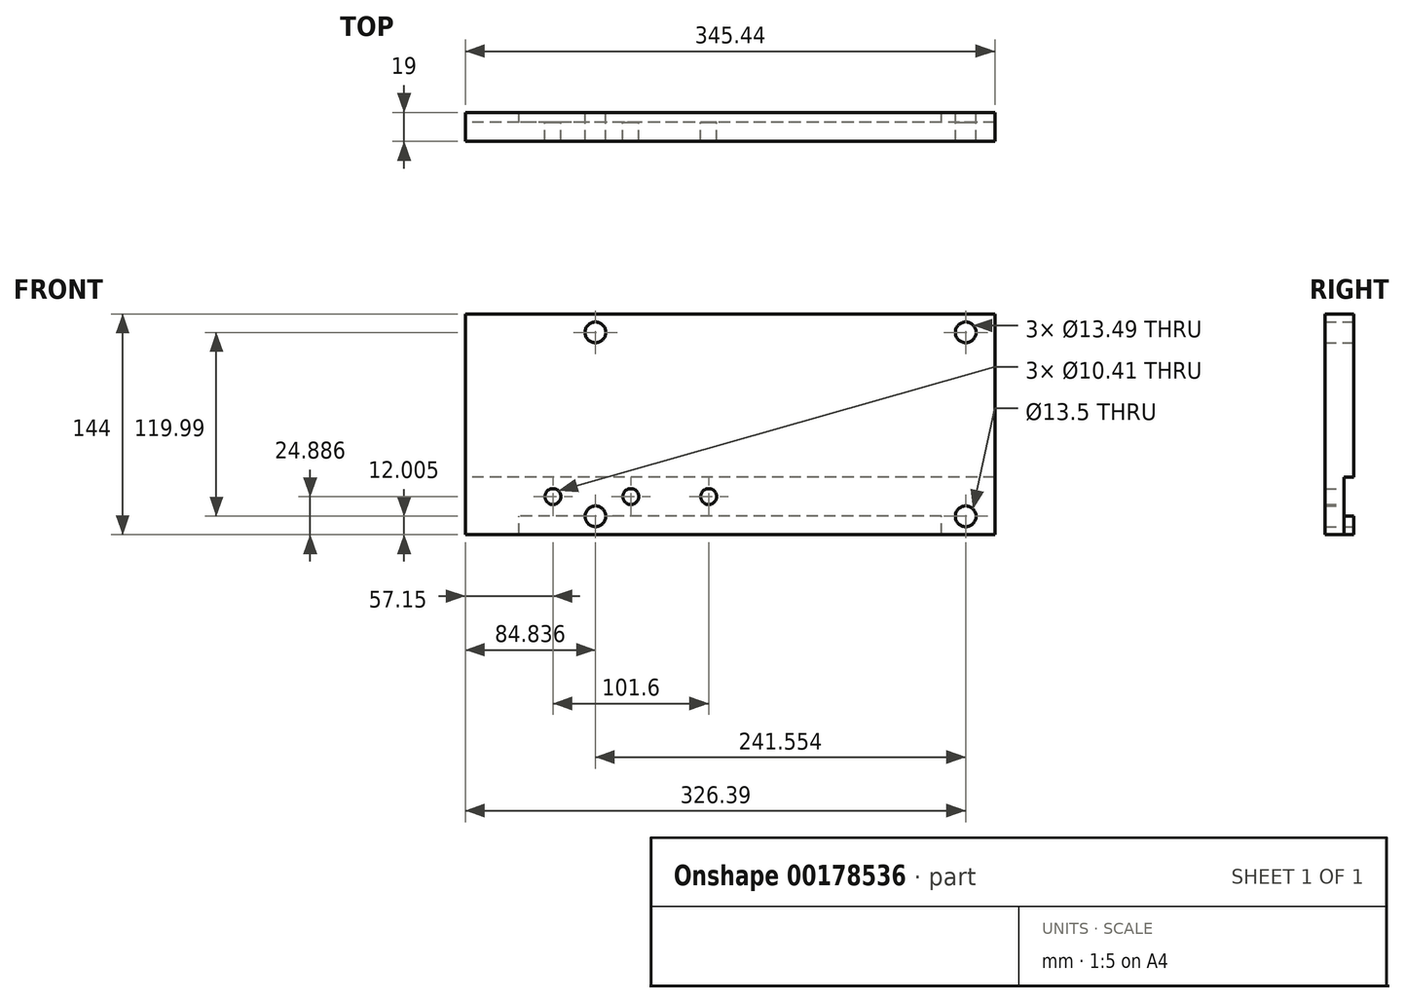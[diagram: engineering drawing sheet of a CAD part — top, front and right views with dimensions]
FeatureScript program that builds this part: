
annotation { "Feature Type Name" : "Feature", "Feature Type Description" : "" }
export const myFeature = defineFeature(function(context is Context, id is Id, definition is map)
    precondition{}
    {
        {
            var Q0;
            Q0=qCreatedBy(makeId("Front.planeOp"),FACE);
            var sketch = newSketch(context, id + "F0", { "sketchPlane" : qUnion([Q0])});
            skLineSegment(sketch, "E0.bottom", {"start": v(172.72, 72) * mm, "end": v(-172.72, 72) * mm});
            skLineSegment(sketch, "E0.top", {"start": v(172.72, -72) * mm, "end": v(-172.72, -72) * mm});
            skLineSegment(sketch, "E0.left", {"start": v(172.72, 72) * mm, "end": v(172.72, -72) * mm});
            skLineSegment(sketch, "E0.right", {"start": v(-172.72, 72) * mm, "end": v(-172.72, -72) * mm});
            skPoint(sketch, "E0.middle", {"position": v(0, 0) * mm});
            skCircle(sketch, "E1", {"center": v(-115.57, -47.11) * mm, "radius": 5.2 * mm});
            skCircle(sketch, "E2.1.0.0", {"center": v(-64.77, -47.11) * mm, "radius": 5.2 * mm});
            skCircle(sketch, "E2.2.0.0", {"center": v(-13.97, -47.11) * mm, "radius": 5.2 * mm});
            skLineSegment(sketch, "E2.direction1", {"start": v(-115.57, -47.11) * mm, "end": v(-64.77, -47.11) * mm, "construction": true});
            skCircle(sketch, "E3", {"center": v(153.67, -60) * mm, "radius": 6.75 * mm});
            skCircle(sketch, "E4", {"center": v(153.67, 60) * mm, "radius": 6.74 * mm});
            skCircle(sketch, "E5", {"center": v(-87.88, -60) * mm, "radius": 6.74 * mm});
            skCircle(sketch, "E6", {"center": v(-87.88, 60) * mm, "radius": 6.74 * mm});
            skSolve(sketch);
        }
        {
            var Q0;
            Q0 = qSketchRegion(id + "F0", true);
            extrude(context, id + "F1", {"entities" : qUnion([Q0]), "depth" : 19 * mm});
        }
        {
            var Q0;
            Q0=makeQuery(id+"F1.opExtrude","SWEPT_FACE",FACE,{"disambiguationData":[OSD([sQuery(id+"F0.wireOp",EDGE,"E0.right")])]});
            var sketch = newSketch(context, id + "F2", { "sketchPlane" : qUnion([Q0])});
            skLineSegment(sketch, "E7.right", {"start": v(6.35, -59.81) * mm, "end": v(6.35, -34.41) * mm});
            skLineSegment(sketch, "E8", {"start": v(6.35, -59.81) * mm, "end": v(0, -59.81) * mm});
            skLineSegment(sketch, "E9", {"start": v(0, -59.81) * mm, "end": v(0, -34.41) * mm});
            skLineSegment(sketch, "E10", {"start": v(0, -34.41) * mm, "end": v(6.35, -34.41) * mm});
            skSolve(sketch);
        }
        {
            var Q0;
            Q0 = qSketchRegion(id + "F2", true);
            extrude(context, id + "F3", {"entities" : qUnion([Q0]), "operationType" : NewBodyOperationType.REMOVE, "endBound" : BoundingType.THROUGH_ALL, "oppositeDirection" : true, "depth" : 25.4 * mm});
        }
        {
            var Q0;
            {var subQ0=sQuery(id+"F0.wireOp",EDGE,"E0.right");var subQ1=sQuery(id+"F0.wireOp",EDGE,"E0.left");var subQ2=sQuery(id+"F0.wireOp",EDGE,"E3");var subQ3=sQuery(id+"F0.wireOp",EDGE,"E0.top");var subQ4=sQuery(id+"F0.wireOp",EDGE,"E5");Q0=makeQuery(id+"F3.boolean.opBoolean","SPLIT",FACE,{"disambiguationData":[TD([makeQuery(id+"F1.opExtrude","SWEPT_FACE",FACE,{"disambiguationData":[OSD([subQ3])]})])],"derivedFrom":makeQuery(id+"F1.opExtrude","CAP_FACE",FACE,{"disambiguationData":[OSD([sQuery(id+"F0.wireOp",EDGE,"E0.bottom"),subQ3,subQ1,subQ0,sQuery(id+"F0.wireOp",EDGE,"E1"),sQuery(id+"F0.wireOp",EDGE,"E2.1.0.0"),sQuery(id+"F0.wireOp",EDGE,"E2.2.0.0"),subQ2,sQuery(id+"F0.wireOp",EDGE,"E4"),subQ4,sQuery(id+"F0.wireOp",EDGE,"E6")])],"isStart":true})});}
            var sketch = newSketch(context, id + "F4", { "sketchPlane" : qUnion([Q0])});
            skLineSegment(sketch, "E11.bottom", {"start": v(-172.72, -72) * mm, "end": v(-137.8, -72) * mm});
            skLineSegment(sketch, "E11.top", {"start": v(-172.72, -34.41) * mm, "end": v(-137.8, -34.41) * mm});
            skLineSegment(sketch, "E11.left", {"start": v(-172.72, -72) * mm, "end": v(-172.72, -34.41) * mm});
            skLineSegment(sketch, "E11.right", {"start": v(-137.8, -72) * mm, "end": v(-137.8, -34.41) * mm});
            skLineSegment(sketch, "E12.bottom", {"start": v(172.72, -72) * mm, "end": v(137.8, -72) * mm});
            skLineSegment(sketch, "E12.top", {"start": v(172.72, -34.41) * mm, "end": v(137.8, -34.41) * mm});
            skLineSegment(sketch, "E12.left", {"start": v(172.72, -72) * mm, "end": v(172.72, -34.41) * mm});
            skLineSegment(sketch, "E12.right", {"start": v(137.8, -72) * mm, "end": v(137.8, -34.41) * mm});
            skSolve(sketch);
        }
        {
            var Q0;
            Q0 = qSketchRegion(id + "F4", true);
            var Q1;
            Q1=makeQuery(id+"F3.boolean.opBoolean","COPY",FACE,{"derivedFrom":makeQuery(id+"F3.opExtrude","SWEPT_FACE",FACE,{"disambiguationData":[OSD([sQuery(id+"F2.wireOp",EDGE,"E7.right")])]})});
            extrude(context, id + "F5", {"entities" : qUnion([Q0]), "operationType" : NewBodyOperationType.REMOVE, "endBound" : BoundingType.UP_TO_SURFACE, "oppositeDirection" : true, "endBoundEntityFace" : qUnion([Q1]), "depth" : 25.4 * mm});
        }
    });
